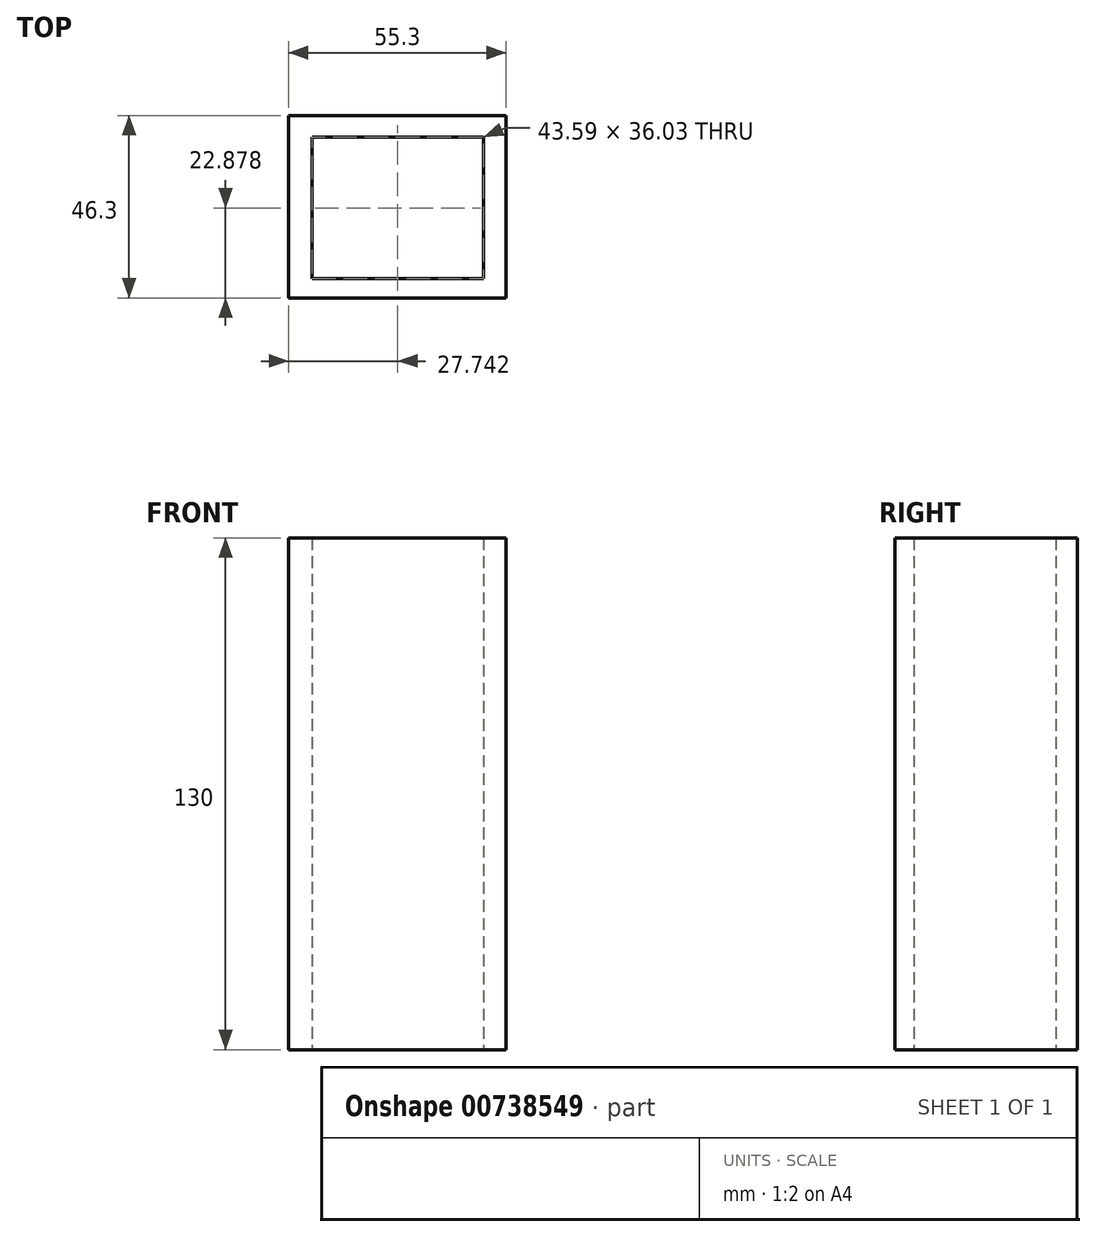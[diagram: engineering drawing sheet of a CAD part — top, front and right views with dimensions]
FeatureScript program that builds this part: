
annotation { "Feature Type Name" : "Feature", "Feature Type Description" : "" }
export const myFeature = defineFeature(function(context is Context, id is Id, definition is map)
    precondition{}
    {
        {
            var Q0;
            Q0=qCreatedBy(makeId("Top.planeOp"),FACE);
            var sketch = newSketch(context, id + "F0", { "sketchPlane" : qUnion([Q0])});
            skLineSegment(sketch, "E0.bottom", {"start": v(0, 0) * mm, "end": v(55.3, 0) * mm});
            skLineSegment(sketch, "E0.top", {"start": v(0, 46.3) * mm, "end": v(55.3, 46.3) * mm});
            skLineSegment(sketch, "E0.left", {"start": v(0, 0) * mm, "end": v(0, 46.3) * mm});
            skLineSegment(sketch, "E0.right", {"start": v(55.3, 0) * mm, "end": v(55.3, 46.3) * mm});
            skLineSegment(sketch, "E1.bottom", {"start": v(5.94, 40.9) * mm, "end": v(49.54, 40.9) * mm});
            skLineSegment(sketch, "E1.top", {"start": v(5.94, 4.86) * mm, "end": v(49.54, 4.86) * mm});
            skLineSegment(sketch, "E1.left", {"start": v(5.94, 40.9) * mm, "end": v(5.94, 4.86) * mm});
            skLineSegment(sketch, "E1.right", {"start": v(49.54, 40.9) * mm, "end": v(49.54, 4.86) * mm});
            skSolve(sketch);
        }
        {
            var Q0;
            Q0 = qSketchRegion(id + "F0", true);
            extrude(context, id + "F1", {"entities" : qUnion([Q0]), "depth" : 130 * mm, "offsetDistance" : 25.4 * mm});
        }
    });
